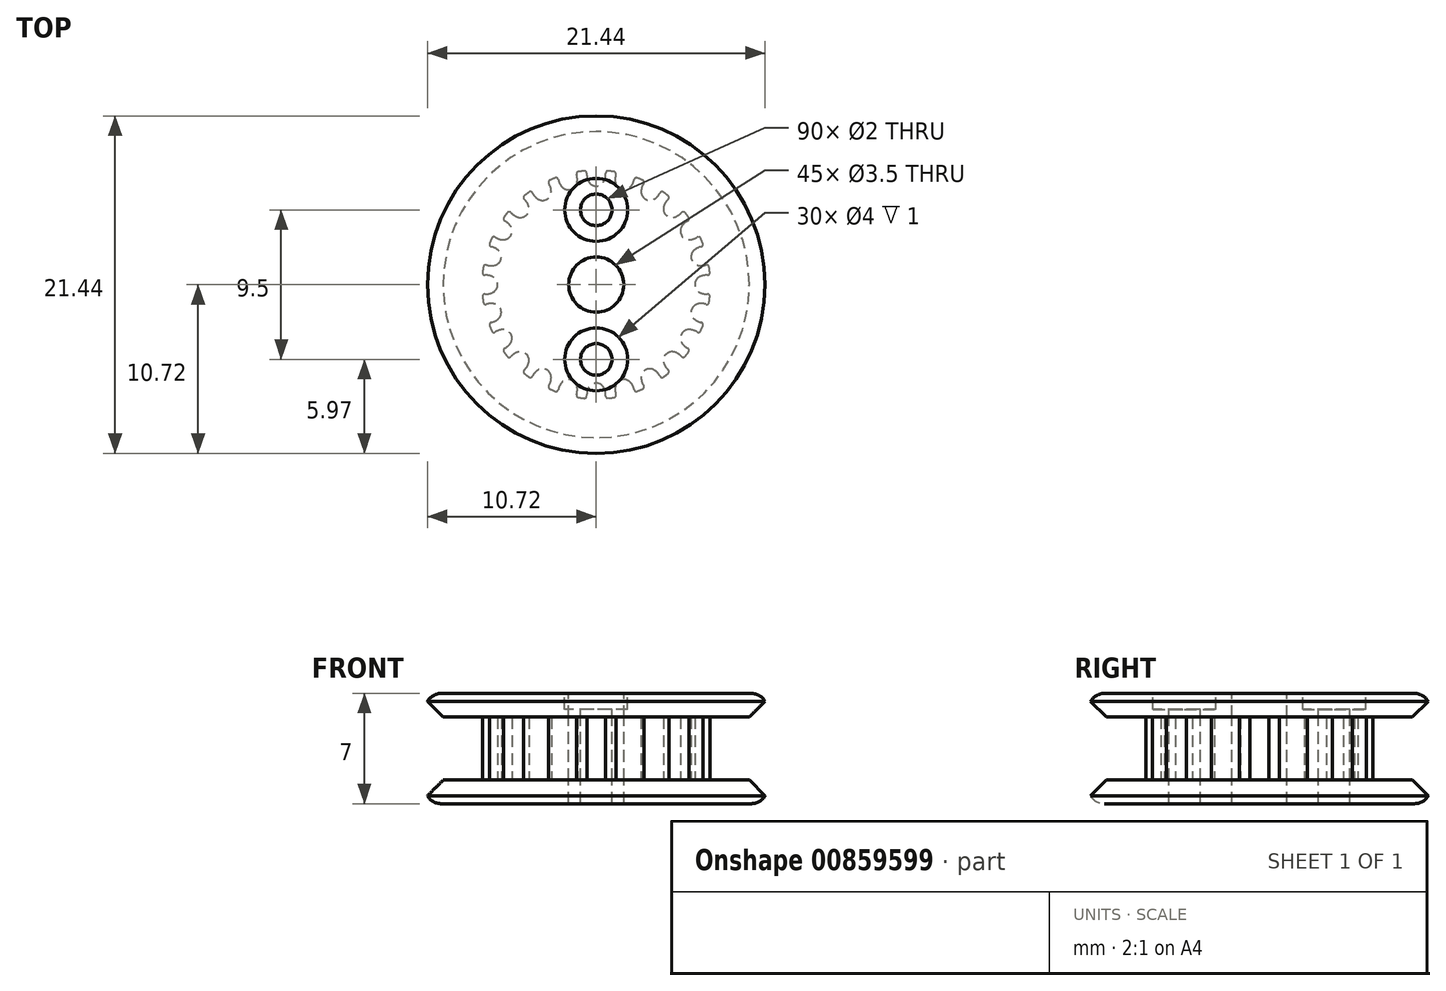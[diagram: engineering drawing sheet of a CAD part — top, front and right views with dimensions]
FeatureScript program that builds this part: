
annotation { "Feature Type Name" : "Feature", "Feature Type Description" : "" }
export const myFeature = defineFeature(function(context is Context, id is Id, definition is map)
    precondition{}
    {
        {
            var Q0;
            Q0=qCreatedBy(makeId("Top.planeOp"),FACE);
            var sketch = newSketch(context, id + "F0", { "sketchPlane" : qUnion([Q0])});
            skCircle(sketch, "E0", {"center": v(0, 0) * mm, "radius": 7.64 * mm, "construction": true});
            skCircle(sketch, "E1", {"center": v(0, 0) * mm, "radius": 6.26 * mm, "construction": true});
            skArc(sketch, "E2", {"start": v(-0.76, 7.22) * mm, "mid": v(-0.95, 7.2) * mm, "end": v(-1.13, 7.17) * mm});
            skArc(sketch, "E3", {"start": v(0, 6.26) * mm, "mid": v(0.3, 6.34) * mm, "end": v(0.5, 6.57) * mm});
            skArc(sketch, "E4", {"start": v(0.76, 7.22) * mm, "mid": v(0.65, 7.18) * mm, "end": v(0.6, 7.06) * mm});
            skArc(sketch, "E5", {"start": v(0.5, 6.57) * mm, "mid": v(0.58, 6.81) * mm, "end": v(0.6, 7.06) * mm});
            skArc(sketch, "E6.MirrorCS", {"start": v(-0.76, 7.22) * mm, "mid": v(-0.65, 7.18) * mm, "end": v(-0.6, 7.06) * mm});
            skArc(sketch, "E7.MirrorCS", {"start": v(-0.5, 6.57) * mm, "mid": v(-0.58, 6.81) * mm, "end": v(-0.6, 7.06) * mm});
            skArc(sketch, "E8.MirrorCS", {"start": v(0, 6.26) * mm, "mid": v(-0.3, 6.34) * mm, "end": v(-0.5, 6.57) * mm});
            skArc(sketch, "E9.1.0", {"start": v(-1.13, 7.17) * mm, "mid": v(-1.23, 7.1) * mm, "end": v(-1.25, 6.98) * mm});
            skArc(sketch, "E9.1.1", {"start": v(-1.22, 6.48) * mm, "mid": v(-1.2, 6.73) * mm, "end": v(-1.25, 6.98) * mm});
            skArc(sketch, "E9.1.2", {"start": v(-1.62, 6.05) * mm, "mid": v(-1.36, 6.2) * mm, "end": v(-1.22, 6.48) * mm});
            skArc(sketch, "E9.1.3", {"start": v(-1.62, 6.05) * mm, "mid": v(-1.93, 6.05) * mm, "end": v(-2.18, 6.22) * mm});
            skArc(sketch, "E9.1.4", {"start": v(-2.18, 6.22) * mm, "mid": v(-2.32, 6.43) * mm, "end": v(-2.4, 6.67) * mm});
            skArc(sketch, "E9.1.5", {"start": v(-2.6, 6.78) * mm, "mid": v(-2.48, 6.77) * mm, "end": v(-2.4, 6.67) * mm});
            skArc(sketch, "E9.2.0", {"start": v(-2.95, 6.63) * mm, "mid": v(-3.03, 6.54) * mm, "end": v(-3.01, 6.42) * mm});
            skArc(sketch, "E9.2.1", {"start": v(-2.85, 5.94) * mm, "mid": v(-2.9, 6.19) * mm, "end": v(-3.01, 6.42) * mm});
            skArc(sketch, "E9.2.2", {"start": v(-3.13, 5.42) * mm, "mid": v(-2.92, 5.64) * mm, "end": v(-2.85, 5.94) * mm});
            skArc(sketch, "E9.2.3", {"start": v(-3.13, 5.42) * mm, "mid": v(-3.43, 5.35) * mm, "end": v(-3.72, 5.44) * mm});
            skArc(sketch, "E9.2.4", {"start": v(-3.72, 5.44) * mm, "mid": v(-3.9, 5.6) * mm, "end": v(-4.05, 5.82) * mm});
            skArc(sketch, "E9.2.5", {"start": v(-4.27, 5.87) * mm, "mid": v(-4.15, 5.9) * mm, "end": v(-4.05, 5.82) * mm});
            skArc(sketch, "E9.3.0", {"start": v(-4.56, 5.65) * mm, "mid": v(-4.62, 5.53) * mm, "end": v(-4.57, 5.42) * mm});
            skArc(sketch, "E9.3.1", {"start": v(-4.3, 5) * mm, "mid": v(-4.4, 5.23) * mm, "end": v(-4.57, 5.42) * mm});
            skArc(sketch, "E9.3.2", {"start": v(-4.43, 4.43) * mm, "mid": v(-4.28, 4.7) * mm, "end": v(-4.3, 5) * mm});
            skArc(sketch, "E9.3.3", {"start": v(-4.43, 4.43) * mm, "mid": v(-4.7, 4.28) * mm, "end": v(-5, 4.3) * mm});
            skArc(sketch, "E9.3.4", {"start": v(-5, 4.3) * mm, "mid": v(-5.23, 4.4) * mm, "end": v(-5.42, 4.57) * mm});
            skArc(sketch, "E9.3.5", {"start": v(-5.65, 4.56) * mm, "mid": v(-5.53, 4.62) * mm, "end": v(-5.42, 4.57) * mm});
            skArc(sketch, "E9.4.0", {"start": v(-5.87, 4.27) * mm, "mid": v(-5.9, 4.15) * mm, "end": v(-5.82, 4.05) * mm});
            skArc(sketch, "E9.4.1", {"start": v(-5.44, 3.72) * mm, "mid": v(-5.6, 3.9) * mm, "end": v(-5.82, 4.05) * mm});
            skArc(sketch, "E9.4.2", {"start": v(-5.42, 3.13) * mm, "mid": v(-5.35, 3.43) * mm, "end": v(-5.44, 3.72) * mm});
            skArc(sketch, "E9.4.3", {"start": v(-5.42, 3.13) * mm, "mid": v(-5.64, 2.92) * mm, "end": v(-5.94, 2.85) * mm});
            skArc(sketch, "E9.4.4", {"start": v(-5.94, 2.85) * mm, "mid": v(-6.19, 2.9) * mm, "end": v(-6.42, 3.01) * mm});
            skArc(sketch, "E9.4.5", {"start": v(-6.63, 2.95) * mm, "mid": v(-6.54, 3.03) * mm, "end": v(-6.42, 3.01) * mm});
            skArc(sketch, "E9.5.0", {"start": v(-6.78, 2.6) * mm, "mid": v(-6.77, 2.48) * mm, "end": v(-6.67, 2.4) * mm});
            skArc(sketch, "E9.5.1", {"start": v(-6.22, 2.18) * mm, "mid": v(-6.43, 2.32) * mm, "end": v(-6.67, 2.4) * mm});
            skArc(sketch, "E9.5.2", {"start": v(-6.05, 1.62) * mm, "mid": v(-6.05, 1.93) * mm, "end": v(-6.22, 2.18) * mm});
            skArc(sketch, "E9.5.3", {"start": v(-6.05, 1.62) * mm, "mid": v(-6.2, 1.36) * mm, "end": v(-6.48, 1.22) * mm});
            skArc(sketch, "E9.5.4", {"start": v(-6.48, 1.22) * mm, "mid": v(-6.73, 1.2) * mm, "end": v(-6.98, 1.25) * mm});
            skArc(sketch, "E9.5.5", {"start": v(-7.17, 1.13) * mm, "mid": v(-7.1, 1.23) * mm, "end": v(-6.98, 1.25) * mm});
            skArc(sketch, "E9.6.0", {"start": v(-7.22, 0.76) * mm, "mid": v(-7.18, 0.65) * mm, "end": v(-7.06, 0.6) * mm});
            skArc(sketch, "E9.6.1", {"start": v(-6.57, 0.5) * mm, "mid": v(-6.81, 0.58) * mm, "end": v(-7.06, 0.6) * mm});
            skArc(sketch, "E9.6.2", {"start": v(-6.26, 0) * mm, "mid": v(-6.34, 0.3) * mm, "end": v(-6.57, 0.5) * mm});
            skArc(sketch, "E9.6.3", {"start": v(-6.26, 0) * mm, "mid": v(-6.34, -0.3) * mm, "end": v(-6.57, -0.5) * mm});
            skArc(sketch, "E9.6.4", {"start": v(-6.57, -0.5) * mm, "mid": v(-6.81, -0.58) * mm, "end": v(-7.06, -0.6) * mm});
            skArc(sketch, "E9.6.5", {"start": v(-7.22, -0.76) * mm, "mid": v(-7.18, -0.65) * mm, "end": v(-7.06, -0.6) * mm});
            skArc(sketch, "E9.7.0", {"start": v(-7.17, -1.13) * mm, "mid": v(-7.1, -1.23) * mm, "end": v(-6.98, -1.25) * mm});
            skArc(sketch, "E9.7.1", {"start": v(-6.48, -1.22) * mm, "mid": v(-6.73, -1.2) * mm, "end": v(-6.98, -1.25) * mm});
            skArc(sketch, "E9.7.2", {"start": v(-6.05, -1.62) * mm, "mid": v(-6.2, -1.36) * mm, "end": v(-6.48, -1.22) * mm});
            skArc(sketch, "E9.7.3", {"start": v(-6.05, -1.62) * mm, "mid": v(-6.05, -1.93) * mm, "end": v(-6.22, -2.18) * mm});
            skArc(sketch, "E9.7.4", {"start": v(-6.22, -2.18) * mm, "mid": v(-6.43, -2.32) * mm, "end": v(-6.67, -2.4) * mm});
            skArc(sketch, "E9.7.5", {"start": v(-6.78, -2.6) * mm, "mid": v(-6.77, -2.48) * mm, "end": v(-6.67, -2.4) * mm});
            skArc(sketch, "E9.8.0", {"start": v(-6.63, -2.95) * mm, "mid": v(-6.54, -3.03) * mm, "end": v(-6.42, -3.01) * mm});
            skArc(sketch, "E9.8.1", {"start": v(-5.94, -2.85) * mm, "mid": v(-6.19, -2.9) * mm, "end": v(-6.42, -3.01) * mm});
            skArc(sketch, "E9.8.2", {"start": v(-5.42, -3.13) * mm, "mid": v(-5.64, -2.92) * mm, "end": v(-5.94, -2.85) * mm});
            skArc(sketch, "E9.8.3", {"start": v(-5.42, -3.13) * mm, "mid": v(-5.35, -3.43) * mm, "end": v(-5.44, -3.72) * mm});
            skArc(sketch, "E9.8.4", {"start": v(-5.44, -3.72) * mm, "mid": v(-5.6, -3.9) * mm, "end": v(-5.82, -4.05) * mm});
            skArc(sketch, "E9.8.5", {"start": v(-5.87, -4.27) * mm, "mid": v(-5.9, -4.15) * mm, "end": v(-5.82, -4.05) * mm});
            skArc(sketch, "E9.9.0", {"start": v(-5.65, -4.56) * mm, "mid": v(-5.53, -4.62) * mm, "end": v(-5.42, -4.57) * mm});
            skArc(sketch, "E9.9.1", {"start": v(-5, -4.3) * mm, "mid": v(-5.23, -4.4) * mm, "end": v(-5.42, -4.57) * mm});
            skArc(sketch, "E9.9.2", {"start": v(-4.43, -4.43) * mm, "mid": v(-4.7, -4.28) * mm, "end": v(-5, -4.3) * mm});
            skArc(sketch, "E9.9.3", {"start": v(-4.43, -4.43) * mm, "mid": v(-4.28, -4.7) * mm, "end": v(-4.3, -5) * mm});
            skArc(sketch, "E9.9.4", {"start": v(-4.3, -5) * mm, "mid": v(-4.4, -5.23) * mm, "end": v(-4.57, -5.42) * mm});
            skArc(sketch, "E9.9.5", {"start": v(-4.56, -5.65) * mm, "mid": v(-4.62, -5.53) * mm, "end": v(-4.57, -5.42) * mm});
            skArc(sketch, "E9.10.0", {"start": v(-4.27, -5.87) * mm, "mid": v(-4.15, -5.9) * mm, "end": v(-4.05, -5.82) * mm});
            skArc(sketch, "E9.10.1", {"start": v(-3.72, -5.44) * mm, "mid": v(-3.9, -5.6) * mm, "end": v(-4.05, -5.82) * mm});
            skArc(sketch, "E9.10.2", {"start": v(-3.13, -5.42) * mm, "mid": v(-3.43, -5.35) * mm, "end": v(-3.72, -5.44) * mm});
            skArc(sketch, "E9.10.3", {"start": v(-3.13, -5.42) * mm, "mid": v(-2.92, -5.64) * mm, "end": v(-2.85, -5.94) * mm});
            skArc(sketch, "E9.10.4", {"start": v(-2.85, -5.94) * mm, "mid": v(-2.9, -6.19) * mm, "end": v(-3.01, -6.42) * mm});
            skArc(sketch, "E9.10.5", {"start": v(-2.95, -6.63) * mm, "mid": v(-3.03, -6.54) * mm, "end": v(-3.01, -6.42) * mm});
            skArc(sketch, "E9.11.0", {"start": v(-2.6, -6.78) * mm, "mid": v(-2.48, -6.77) * mm, "end": v(-2.4, -6.67) * mm});
            skArc(sketch, "E9.11.1", {"start": v(-2.18, -6.22) * mm, "mid": v(-2.32, -6.43) * mm, "end": v(-2.4, -6.67) * mm});
            skArc(sketch, "E9.11.2", {"start": v(-1.62, -6.05) * mm, "mid": v(-1.93, -6.05) * mm, "end": v(-2.18, -6.22) * mm});
            skArc(sketch, "E9.11.3", {"start": v(-1.62, -6.05) * mm, "mid": v(-1.36, -6.2) * mm, "end": v(-1.22, -6.48) * mm});
            skArc(sketch, "E9.11.4", {"start": v(-1.22, -6.48) * mm, "mid": v(-1.2, -6.73) * mm, "end": v(-1.25, -6.98) * mm});
            skArc(sketch, "E9.11.5", {"start": v(-1.13, -7.17) * mm, "mid": v(-1.23, -7.1) * mm, "end": v(-1.25, -6.98) * mm});
            skArc(sketch, "E9.12.0", {"start": v(-0.76, -7.22) * mm, "mid": v(-0.65, -7.18) * mm, "end": v(-0.6, -7.06) * mm});
            skArc(sketch, "E9.12.1", {"start": v(-0.5, -6.57) * mm, "mid": v(-0.58, -6.81) * mm, "end": v(-0.6, -7.06) * mm});
            skArc(sketch, "E9.12.2", {"start": v(0, -6.26) * mm, "mid": v(-0.3, -6.34) * mm, "end": v(-0.5, -6.57) * mm});
            skArc(sketch, "E9.12.3", {"start": v(0, -6.26) * mm, "mid": v(0.3, -6.34) * mm, "end": v(0.5, -6.57) * mm});
            skArc(sketch, "E9.12.4", {"start": v(0.5, -6.57) * mm, "mid": v(0.58, -6.81) * mm, "end": v(0.6, -7.06) * mm});
            skArc(sketch, "E9.12.5", {"start": v(0.76, -7.22) * mm, "mid": v(0.65, -7.18) * mm, "end": v(0.6, -7.06) * mm});
            skArc(sketch, "E9.13.0", {"start": v(1.13, -7.17) * mm, "mid": v(1.23, -7.1) * mm, "end": v(1.25, -6.98) * mm});
            skArc(sketch, "E9.13.1", {"start": v(1.22, -6.48) * mm, "mid": v(1.2, -6.73) * mm, "end": v(1.25, -6.98) * mm});
            skArc(sketch, "E9.13.2", {"start": v(1.62, -6.05) * mm, "mid": v(1.36, -6.2) * mm, "end": v(1.22, -6.48) * mm});
            skArc(sketch, "E9.13.3", {"start": v(1.62, -6.05) * mm, "mid": v(1.93, -6.05) * mm, "end": v(2.18, -6.22) * mm});
            skArc(sketch, "E9.13.4", {"start": v(2.18, -6.22) * mm, "mid": v(2.32, -6.43) * mm, "end": v(2.4, -6.67) * mm});
            skArc(sketch, "E9.13.5", {"start": v(2.6, -6.78) * mm, "mid": v(2.48, -6.77) * mm, "end": v(2.4, -6.67) * mm});
            skArc(sketch, "E9.14.0", {"start": v(2.95, -6.63) * mm, "mid": v(3.03, -6.54) * mm, "end": v(3.01, -6.42) * mm});
            skArc(sketch, "E9.14.1", {"start": v(2.85, -5.94) * mm, "mid": v(2.9, -6.19) * mm, "end": v(3.01, -6.42) * mm});
            skArc(sketch, "E9.14.2", {"start": v(3.13, -5.42) * mm, "mid": v(2.92, -5.64) * mm, "end": v(2.85, -5.94) * mm});
            skArc(sketch, "E9.14.3", {"start": v(3.13, -5.42) * mm, "mid": v(3.43, -5.35) * mm, "end": v(3.72, -5.44) * mm});
            skArc(sketch, "E9.14.4", {"start": v(3.72, -5.44) * mm, "mid": v(3.9, -5.6) * mm, "end": v(4.05, -5.82) * mm});
            skArc(sketch, "E9.14.5", {"start": v(4.27, -5.87) * mm, "mid": v(4.15, -5.9) * mm, "end": v(4.05, -5.82) * mm});
            skArc(sketch, "E9.15.0", {"start": v(4.56, -5.65) * mm, "mid": v(4.62, -5.53) * mm, "end": v(4.57, -5.42) * mm});
            skArc(sketch, "E9.15.1", {"start": v(4.3, -5) * mm, "mid": v(4.4, -5.23) * mm, "end": v(4.57, -5.42) * mm});
            skArc(sketch, "E9.15.2", {"start": v(4.43, -4.43) * mm, "mid": v(4.28, -4.7) * mm, "end": v(4.3, -5) * mm});
            skArc(sketch, "E9.15.3", {"start": v(4.43, -4.43) * mm, "mid": v(4.7, -4.28) * mm, "end": v(5, -4.3) * mm});
            skArc(sketch, "E9.15.4", {"start": v(5, -4.3) * mm, "mid": v(5.23, -4.4) * mm, "end": v(5.42, -4.57) * mm});
            skArc(sketch, "E9.15.5", {"start": v(5.65, -4.56) * mm, "mid": v(5.53, -4.62) * mm, "end": v(5.42, -4.57) * mm});
            skArc(sketch, "E9.16.0", {"start": v(5.87, -4.27) * mm, "mid": v(5.9, -4.15) * mm, "end": v(5.82, -4.05) * mm});
            skArc(sketch, "E9.16.1", {"start": v(5.44, -3.72) * mm, "mid": v(5.6, -3.9) * mm, "end": v(5.82, -4.05) * mm});
            skArc(sketch, "E9.16.2", {"start": v(5.42, -3.13) * mm, "mid": v(5.35, -3.43) * mm, "end": v(5.44, -3.72) * mm});
            skArc(sketch, "E9.16.3", {"start": v(5.42, -3.13) * mm, "mid": v(5.64, -2.92) * mm, "end": v(5.94, -2.85) * mm});
            skArc(sketch, "E9.16.4", {"start": v(5.94, -2.85) * mm, "mid": v(6.19, -2.9) * mm, "end": v(6.42, -3.01) * mm});
            skArc(sketch, "E9.16.5", {"start": v(6.63, -2.95) * mm, "mid": v(6.54, -3.03) * mm, "end": v(6.42, -3.01) * mm});
            skArc(sketch, "E9.17.0", {"start": v(6.78, -2.6) * mm, "mid": v(6.77, -2.48) * mm, "end": v(6.67, -2.4) * mm});
            skArc(sketch, "E9.17.1", {"start": v(6.22, -2.18) * mm, "mid": v(6.43, -2.32) * mm, "end": v(6.67, -2.4) * mm});
            skArc(sketch, "E9.17.2", {"start": v(6.05, -1.62) * mm, "mid": v(6.05, -1.93) * mm, "end": v(6.22, -2.18) * mm});
            skArc(sketch, "E9.17.3", {"start": v(6.05, -1.62) * mm, "mid": v(6.2, -1.36) * mm, "end": v(6.48, -1.22) * mm});
            skArc(sketch, "E9.17.4", {"start": v(6.48, -1.22) * mm, "mid": v(6.73, -1.2) * mm, "end": v(6.98, -1.25) * mm});
            skArc(sketch, "E9.17.5", {"start": v(7.17, -1.13) * mm, "mid": v(7.1, -1.23) * mm, "end": v(6.98, -1.25) * mm});
            skArc(sketch, "E9.18.0", {"start": v(7.22, -0.76) * mm, "mid": v(7.18, -0.65) * mm, "end": v(7.06, -0.6) * mm});
            skArc(sketch, "E9.18.1", {"start": v(6.57, -0.5) * mm, "mid": v(6.81, -0.58) * mm, "end": v(7.06, -0.6) * mm});
            skArc(sketch, "E9.18.2", {"start": v(6.26, 0) * mm, "mid": v(6.34, -0.3) * mm, "end": v(6.57, -0.5) * mm});
            skArc(sketch, "E9.18.3", {"start": v(6.26, 0) * mm, "mid": v(6.34, 0.3) * mm, "end": v(6.57, 0.5) * mm});
            skArc(sketch, "E9.18.4", {"start": v(6.57, 0.5) * mm, "mid": v(6.81, 0.58) * mm, "end": v(7.06, 0.6) * mm});
            skArc(sketch, "E9.18.5", {"start": v(7.22, 0.76) * mm, "mid": v(7.18, 0.65) * mm, "end": v(7.06, 0.6) * mm});
            skArc(sketch, "E9.19.0", {"start": v(7.17, 1.13) * mm, "mid": v(7.1, 1.23) * mm, "end": v(6.98, 1.25) * mm});
            skArc(sketch, "E9.19.1", {"start": v(6.48, 1.22) * mm, "mid": v(6.73, 1.2) * mm, "end": v(6.98, 1.25) * mm});
            skArc(sketch, "E9.19.2", {"start": v(6.05, 1.62) * mm, "mid": v(6.2, 1.36) * mm, "end": v(6.48, 1.22) * mm});
            skArc(sketch, "E9.19.3", {"start": v(6.05, 1.62) * mm, "mid": v(6.05, 1.93) * mm, "end": v(6.22, 2.18) * mm});
            skArc(sketch, "E9.19.4", {"start": v(6.22, 2.18) * mm, "mid": v(6.43, 2.32) * mm, "end": v(6.67, 2.4) * mm});
            skArc(sketch, "E9.19.5", {"start": v(6.78, 2.6) * mm, "mid": v(6.77, 2.48) * mm, "end": v(6.67, 2.4) * mm});
            skArc(sketch, "E9.20.0", {"start": v(6.63, 2.95) * mm, "mid": v(6.54, 3.03) * mm, "end": v(6.42, 3.01) * mm});
            skArc(sketch, "E9.20.1", {"start": v(5.94, 2.85) * mm, "mid": v(6.19, 2.9) * mm, "end": v(6.42, 3.01) * mm});
            skArc(sketch, "E9.20.2", {"start": v(5.42, 3.13) * mm, "mid": v(5.64, 2.92) * mm, "end": v(5.94, 2.85) * mm});
            skArc(sketch, "E9.20.3", {"start": v(5.42, 3.13) * mm, "mid": v(5.35, 3.43) * mm, "end": v(5.44, 3.72) * mm});
            skArc(sketch, "E9.20.4", {"start": v(5.44, 3.72) * mm, "mid": v(5.6, 3.9) * mm, "end": v(5.82, 4.05) * mm});
            skArc(sketch, "E9.20.5", {"start": v(5.87, 4.27) * mm, "mid": v(5.9, 4.15) * mm, "end": v(5.82, 4.05) * mm});
            skArc(sketch, "E9.21.0", {"start": v(5.65, 4.56) * mm, "mid": v(5.53, 4.62) * mm, "end": v(5.42, 4.57) * mm});
            skArc(sketch, "E9.21.1", {"start": v(5, 4.3) * mm, "mid": v(5.23, 4.4) * mm, "end": v(5.42, 4.57) * mm});
            skArc(sketch, "E9.21.2", {"start": v(4.43, 4.43) * mm, "mid": v(4.7, 4.28) * mm, "end": v(5, 4.3) * mm});
            skArc(sketch, "E9.21.3", {"start": v(4.43, 4.43) * mm, "mid": v(4.28, 4.7) * mm, "end": v(4.3, 5) * mm});
            skArc(sketch, "E9.21.4", {"start": v(4.3, 5) * mm, "mid": v(4.4, 5.23) * mm, "end": v(4.57, 5.42) * mm});
            skArc(sketch, "E9.21.5", {"start": v(4.56, 5.65) * mm, "mid": v(4.62, 5.53) * mm, "end": v(4.57, 5.42) * mm});
            skArc(sketch, "E9.22.0", {"start": v(4.27, 5.87) * mm, "mid": v(4.15, 5.9) * mm, "end": v(4.05, 5.82) * mm});
            skArc(sketch, "E9.22.1", {"start": v(3.72, 5.44) * mm, "mid": v(3.9, 5.6) * mm, "end": v(4.05, 5.82) * mm});
            skArc(sketch, "E9.22.2", {"start": v(3.13, 5.42) * mm, "mid": v(3.43, 5.35) * mm, "end": v(3.72, 5.44) * mm});
            skArc(sketch, "E9.22.3", {"start": v(3.13, 5.42) * mm, "mid": v(2.92, 5.64) * mm, "end": v(2.85, 5.94) * mm});
            skArc(sketch, "E9.22.4", {"start": v(2.85, 5.94) * mm, "mid": v(2.9, 6.19) * mm, "end": v(3.01, 6.42) * mm});
            skArc(sketch, "E9.22.5", {"start": v(2.95, 6.63) * mm, "mid": v(3.03, 6.54) * mm, "end": v(3.01, 6.42) * mm});
            skArc(sketch, "E9.23.0", {"start": v(2.6, 6.78) * mm, "mid": v(2.48, 6.77) * mm, "end": v(2.4, 6.67) * mm});
            skArc(sketch, "E9.23.1", {"start": v(2.18, 6.22) * mm, "mid": v(2.32, 6.43) * mm, "end": v(2.4, 6.67) * mm});
            skArc(sketch, "E9.23.2", {"start": v(1.62, 6.05) * mm, "mid": v(1.93, 6.05) * mm, "end": v(2.18, 6.22) * mm});
            skArc(sketch, "E9.23.3", {"start": v(1.62, 6.05) * mm, "mid": v(1.36, 6.2) * mm, "end": v(1.22, 6.48) * mm});
            skArc(sketch, "E9.23.4", {"start": v(1.22, 6.48) * mm, "mid": v(1.2, 6.73) * mm, "end": v(1.25, 6.98) * mm});
            skArc(sketch, "E9.23.5", {"start": v(1.13, 7.17) * mm, "mid": v(1.23, 7.1) * mm, "end": v(1.25, 6.98) * mm});
            skArc(sketch, "E10.trimOffspring", {"start": v(1.13, 7.17) * mm, "mid": v(0.95, 7.2) * mm, "end": v(0.76, 7.22) * mm});
            skArc(sketch, "E11.trimOffspring", {"start": v(2.95, 6.63) * mm, "mid": v(2.78, 6.7) * mm, "end": v(2.6, 6.78) * mm});
            skArc(sketch, "E12.trimOffspring", {"start": v(4.56, 5.65) * mm, "mid": v(4.42, 5.76) * mm, "end": v(4.27, 5.87) * mm});
            skArc(sketch, "E13.trimOffspring", {"start": v(5.87, 4.27) * mm, "mid": v(5.76, 4.42) * mm, "end": v(5.65, 4.56) * mm});
            skArc(sketch, "E14.trimOffspring", {"start": v(6.78, 2.6) * mm, "mid": v(6.7, 2.78) * mm, "end": v(6.63, 2.95) * mm});
            skArc(sketch, "E15.trimOffspring", {"start": v(7.22, 0.76) * mm, "mid": v(7.2, 0.95) * mm, "end": v(7.17, 1.13) * mm});
            skArc(sketch, "E16.trimOffspring", {"start": v(7.17, -1.13) * mm, "mid": v(7.2, -0.95) * mm, "end": v(7.22, -0.76) * mm});
            skArc(sketch, "E17.trimOffspring", {"start": v(6.63, -2.95) * mm, "mid": v(6.7, -2.78) * mm, "end": v(6.78, -2.6) * mm});
            skArc(sketch, "E18.trimOffspring", {"start": v(5.65, -4.56) * mm, "mid": v(5.76, -4.42) * mm, "end": v(5.87, -4.27) * mm});
            skArc(sketch, "E19.trimOffspring", {"start": v(4.27, -5.87) * mm, "mid": v(4.42, -5.76) * mm, "end": v(4.56, -5.65) * mm});
            skArc(sketch, "E20.trimOffspring", {"start": v(2.6, -6.78) * mm, "mid": v(2.78, -6.7) * mm, "end": v(2.95, -6.63) * mm});
            skArc(sketch, "E21.trimOffspring", {"start": v(0.76, -7.22) * mm, "mid": v(0.95, -7.2) * mm, "end": v(1.13, -7.17) * mm});
            skArc(sketch, "E22.trimOffspring", {"start": v(-1.13, -7.17) * mm, "mid": v(-0.95, -7.2) * mm, "end": v(-0.76, -7.22) * mm});
            skArc(sketch, "E23.trimOffspring", {"start": v(-2.95, -6.63) * mm, "mid": v(-2.78, -6.7) * mm, "end": v(-2.6, -6.78) * mm});
            skArc(sketch, "E24.trimOffspring", {"start": v(-4.56, -5.65) * mm, "mid": v(-4.42, -5.76) * mm, "end": v(-4.27, -5.87) * mm});
            skArc(sketch, "E25.trimOffspring", {"start": v(-5.87, -4.27) * mm, "mid": v(-5.76, -4.42) * mm, "end": v(-5.65, -4.56) * mm});
            skArc(sketch, "E26.trimOffspring", {"start": v(-6.78, -2.6) * mm, "mid": v(-6.7, -2.78) * mm, "end": v(-6.63, -2.95) * mm});
            skArc(sketch, "E27.trimOffspring", {"start": v(-7.22, -0.76) * mm, "mid": v(-7.2, -0.95) * mm, "end": v(-7.17, -1.13) * mm});
            skArc(sketch, "E28.trimOffspring", {"start": v(-7.17, 1.13) * mm, "mid": v(-7.2, 0.95) * mm, "end": v(-7.22, 0.76) * mm});
            skArc(sketch, "E29.trimOffspring", {"start": v(-6.63, 2.95) * mm, "mid": v(-6.7, 2.78) * mm, "end": v(-6.78, 2.6) * mm});
            skArc(sketch, "E30.trimOffspring", {"start": v(-5.65, 4.56) * mm, "mid": v(-5.76, 4.42) * mm, "end": v(-5.87, 4.27) * mm});
            skArc(sketch, "E31.trimOffspring", {"start": v(-4.27, 5.87) * mm, "mid": v(-4.42, 5.76) * mm, "end": v(-4.56, 5.65) * mm});
            skArc(sketch, "E32.trimOffspring", {"start": v(-2.6, 6.78) * mm, "mid": v(-2.78, 6.7) * mm, "end": v(-2.95, 6.63) * mm});
            skSolve(sketch);
        }
        {
            var Q0;
            Q0 = qSketchRegion(id + "F0", true);
            extrude(context, id + "F1", {"entities" : qUnion([Q0]), "depth" : 2 * mm, "offsetDistance" : 25 * mm, "hasSecondDirection" : true, "secondDirectionOppositeDirection" : true, "secondDirectionDepth" : 2 * mm});
        }
        {
            var Q0;
            Q0=qCreatedBy(makeId("Right.planeOp"),FACE);
            var sketch = newSketch(context, id + "F2", { "sketchPlane" : qUnion([Q0])});
            skPoint(sketch, "E33.0", {"position": v(0, 2) * mm});
            skPoint(sketch, "E34.0", {"position": v(7.22, 2) * mm});
            skLineSegment(sketch, "E35", {"start": v(0, 2) * mm, "end": v(7.22, 2) * mm});
            skLineSegment(sketch, "E36", {"start": v(10.72, 2) * mm, "end": v(10.72, 3.5) * mm});
            skLineSegment(sketch, "E37", {"start": v(10.72, 3.5) * mm, "end": v(0, 3.5) * mm});
            skLineSegment(sketch, "E38", {"start": v(0, 3.5) * mm, "end": v(0, 2) * mm});
            skLineSegment(sketch, "E39", {"start": v(10.72, 2) * mm, "end": v(7.22, 2) * mm});
            skLineSegment(sketch, "E40.MirrorCS", {"start": v(0, -3.5) * mm, "end": v(0, -2) * mm});
            skLineSegment(sketch, "E41.MirrorCS", {"start": v(10.72, -2) * mm, "end": v(10.72, -3.5) * mm});
            skLineSegment(sketch, "E42.MirrorCS", {"start": v(10.72, -2) * mm, "end": v(7.22, -2) * mm});
            skPoint(sketch, "E43.MirrorP", {"position": v(7.22, -2) * mm});
            skPoint(sketch, "E44.MirrorP", {"position": v(0, -2) * mm});
            skLineSegment(sketch, "E45.MirrorCS", {"start": v(10.72, -3.5) * mm, "end": v(0, -3.5) * mm});
            skLineSegment(sketch, "E46.MirrorCS", {"start": v(0, -2) * mm, "end": v(7.22, -2) * mm});
            skSolve(sketch);
        }
        {
            var Q0;
            Q0 = qSketchRegion(id + "F2", true);
            var Q1;
            Q1=sQuery(id+"F2.wireOp",EDGE,"E38");
            revolve(context, id + "F3", {"surfaceOperationType" : NewSurfaceOperationType.NEW, "entities" : qUnion([Q0]), "axis" : qUnion([Q1]), "revolveType" : RevolveType.FULL});
        }
        {
            var Q0;
            Q0=makeQuery(id+"F3.opRevolve","SWEPT_EDGE",EDGE,{"disambiguationData":[OSD([sQuery(id+"F2.wireOp",EDGE,"E36"),sQuery(id+"F2.wireOp",EDGE,"E39")])]});
            var Q1;
            Q1=makeQuery(id+"F3.opRevolve","SWEPT_EDGE",EDGE,{"disambiguationData":[OSD([sQuery(id+"F2.wireOp",EDGE,"E41.MirrorCS"),sQuery(id+"F2.wireOp",EDGE,"E42.MirrorCS")])]});
            chamfer(context, id + "F4", {"entities" : qUnion([Q0, Q1]), "width" : 1 * mm, "tangentPropagation" : true});
        }
        {
            var Q0;
            Q0=makeQuery(id+"F3.opRevolve","SWEPT_EDGE",EDGE,{"disambiguationData":[OSD([sQuery(id+"F2.wireOp",EDGE,"E36"),sQuery(id+"F2.wireOp",EDGE,"E37")])]});
            var Q1;
            Q1=makeQuery(id+"F3.opRevolve","SWEPT_EDGE",EDGE,{"disambiguationData":[OSD([sQuery(id+"F2.wireOp",EDGE,"E41.MirrorCS"),sQuery(id+"F2.wireOp",EDGE,"E45.MirrorCS")])]});
            fillet(context, id + "F5", {"entities" : qUnion([Q0, Q1]), "radius" : 1 * mm, "tangentPropagation" : true, "allowEdgeOverflow" : false});
        }
        {
            var Q0;
            Q0=makeQuery(id+"F3.opRevolve","SWEPT_FACE",FACE,{"disambiguationData":[OSD([sQuery(id+"F2.wireOp",EDGE,"E37")])]});
            var sketch = newSketch(context, id + "F6", { "sketchPlane" : qUnion([Q0])});
            skCircle(sketch, "E47", {"center": v(0, 0) * mm, "radius": 1.75 * mm});
            skCircle(sketch, "E48", {"center": v(0, -4.75) * mm, "radius": 1 * mm});
            skCircle(sketch, "E49.MirrorC", {"center": v(0, 4.75) * mm, "radius": 1 * mm});
            skSolve(sketch);
        }
        {
            var Q0;
            Q0 = qSketchRegion(id + "F6", true);
            extrude(context, id + "F7", {"entities" : qUnion([Q0]), "operationType" : NewBodyOperationType.REMOVE, "endBound" : BoundingType.THROUGH_ALL, "oppositeDirection" : true, "depth" : 25 * mm, "offsetDistance" : 25 * mm});
        }
        {
            var Q0;
            Q0=makeQuery(id+"F3.opRevolve","SWEPT_FACE",FACE,{"disambiguationData":[OSD([sQuery(id+"F2.wireOp",EDGE,"E37")])]});
            var sketch = newSketch(context, id + "F8", { "sketchPlane" : qUnion([Q0])});
            skCircle(sketch, "E50", {"center": v(0, 4.75) * mm, "radius": 2 * mm});
            skCircle(sketch, "E51", {"center": v(0, -4.75) * mm, "radius": 2 * mm});
            skSolve(sketch);
        }
        {
            var Q0;
            Q0 = qSketchRegion(id + "F8", true);
            extrude(context, id + "F9", {"entities" : qUnion([Q0]), "operationType" : NewBodyOperationType.REMOVE, "oppositeDirection" : true, "depth" : 1 * mm, "offsetDistance" : 25 * mm});
        }
    });
